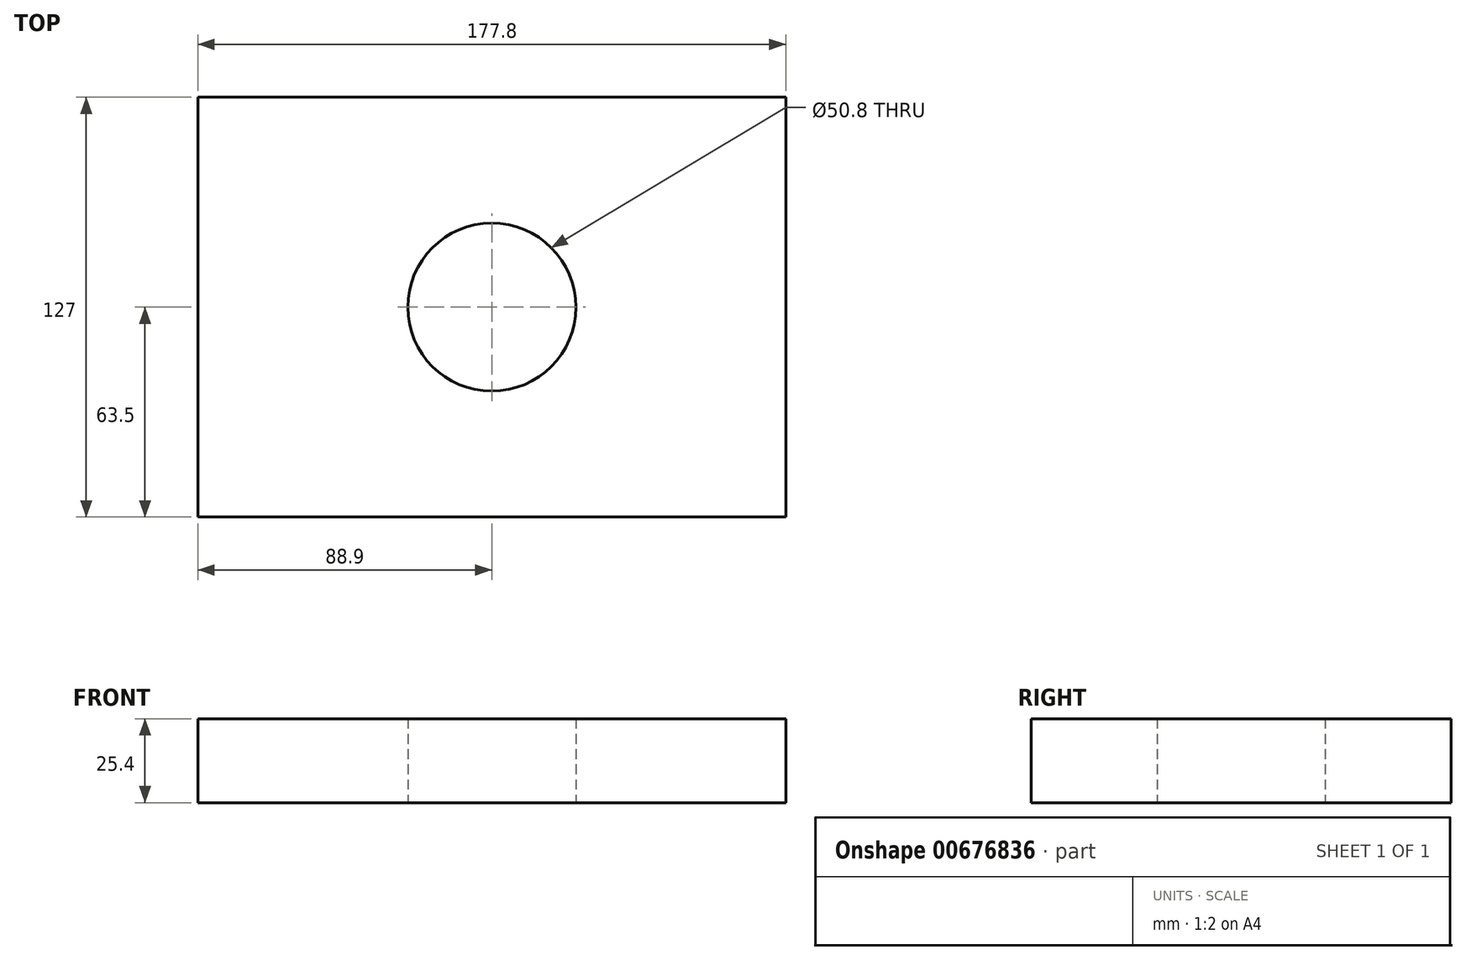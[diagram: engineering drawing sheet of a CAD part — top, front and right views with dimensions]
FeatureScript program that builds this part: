
annotation { "Feature Type Name" : "Feature", "Feature Type Description" : "" }
export const myFeature = defineFeature(function(context is Context, id is Id, definition is map)
    precondition{}
    {
        {
            var Q0;
            Q0=qCreatedBy(makeId("Top.planeOp"),FACE);
            var sketch = newSketch(context, id + "F0", { "sketchPlane" : qUnion([Q0])});
            skLineSegment(sketch, "E0.bottom", {"start": v(-88.9, -63.5) * mm, "end": v(88.9, -63.5) * mm});
            skLineSegment(sketch, "E0.top", {"start": v(-88.9, 63.5) * mm, "end": v(88.9, 63.5) * mm});
            skLineSegment(sketch, "E0.left", {"start": v(-88.9, -63.5) * mm, "end": v(-88.9, 63.5) * mm});
            skLineSegment(sketch, "E0.right", {"start": v(88.9, -63.5) * mm, "end": v(88.9, 63.5) * mm});
            skPoint(sketch, "E0.middle", {"position": v(0, 0) * mm});
            skCircle(sketch, "E1", {"center": v(0, 0) * mm, "radius": 25.4 * mm});
            skSolve(sketch);
        }
        {
            var Q0;
            Q0=makeQuery(id+"F0.imprint","IMPRINT",FACE,{"disambiguationData":[TD([[makeQuery(id+"F0.imprint","IMPRINT",EDGE,{"derivedFrom":sQuery(id+"F0.wireOp",EDGE,"E0.bottom")}),1.0]])]});
            extrude(context, id + "F1", {"entities" : qUnion([Q0]), "depth" : 25.4 * mm, "offsetDistance" : 25.4 * mm});
        }
    });
